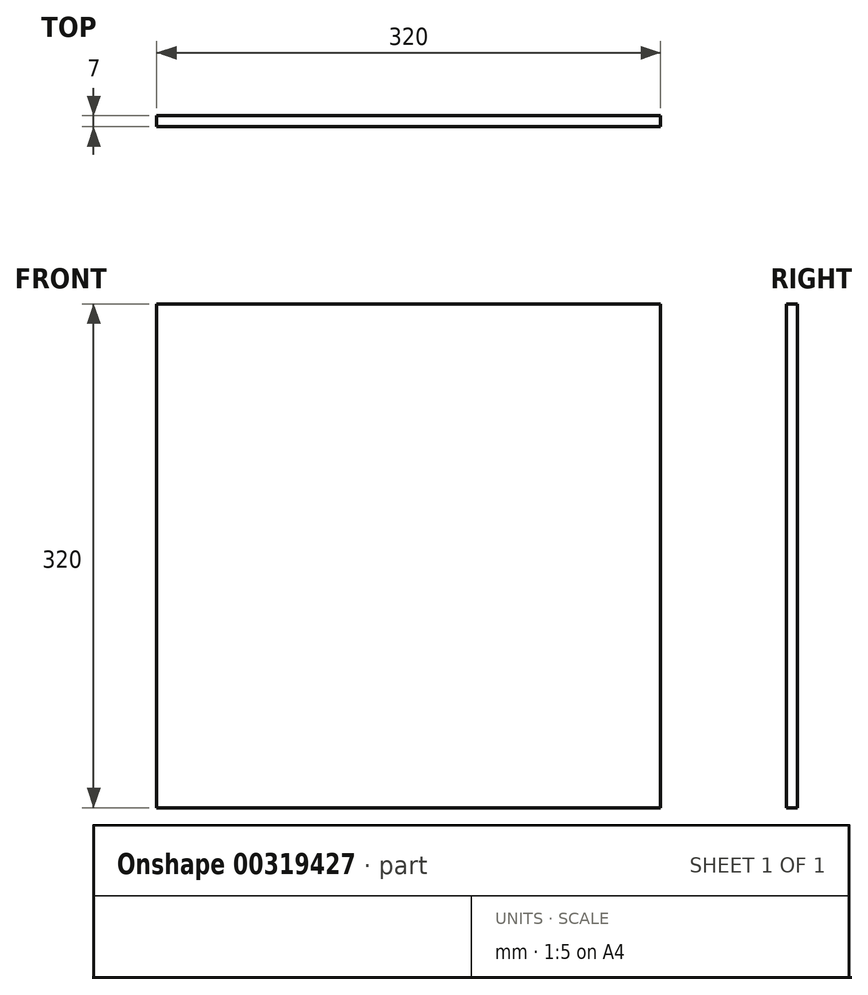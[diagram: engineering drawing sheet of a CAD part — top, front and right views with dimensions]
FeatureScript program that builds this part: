
annotation { "Feature Type Name" : "Feature", "Feature Type Description" : "" }
export const myFeature = defineFeature(function(context is Context, id is Id, definition is map)
    precondition{}
    {
        {
            var Q0;
            Q0=qCreatedBy(makeId("Front.planeOp"),FACE);
            var sketch = newSketch(context, id + "F0", { "sketchPlane" : qUnion([Q0])});
            skLineSegment(sketch, "E0.bottom", {"start": v(-137.88, 171.03) * mm, "end": v(182.12, 171.03) * mm});
            skLineSegment(sketch, "E0.top", {"start": v(-137.88, -148.97) * mm, "end": v(182.12, -148.97) * mm});
            skLineSegment(sketch, "E0.left", {"start": v(-137.88, 171.03) * mm, "end": v(-137.88, -148.97) * mm});
            skLineSegment(sketch, "E0.right", {"start": v(182.12, 171.03) * mm, "end": v(182.12, -148.97) * mm});
            skSolve(sketch);
        }
        {
            var Q0;
            Q0=makeQuery(id+"F0.imprint","IMPRINT",FACE,{"disambiguationData":[TD([[makeQuery(id+"F0.imprint","IMPRINT",EDGE,{"derivedFrom":sQuery(id+"F0.wireOp",EDGE,"E0.bottom")}),-1.0]])]});
            extrude(context, id + "F1", {"entities" : qUnion([Q0]), "depth" : 7 * mm});
        }
    });
